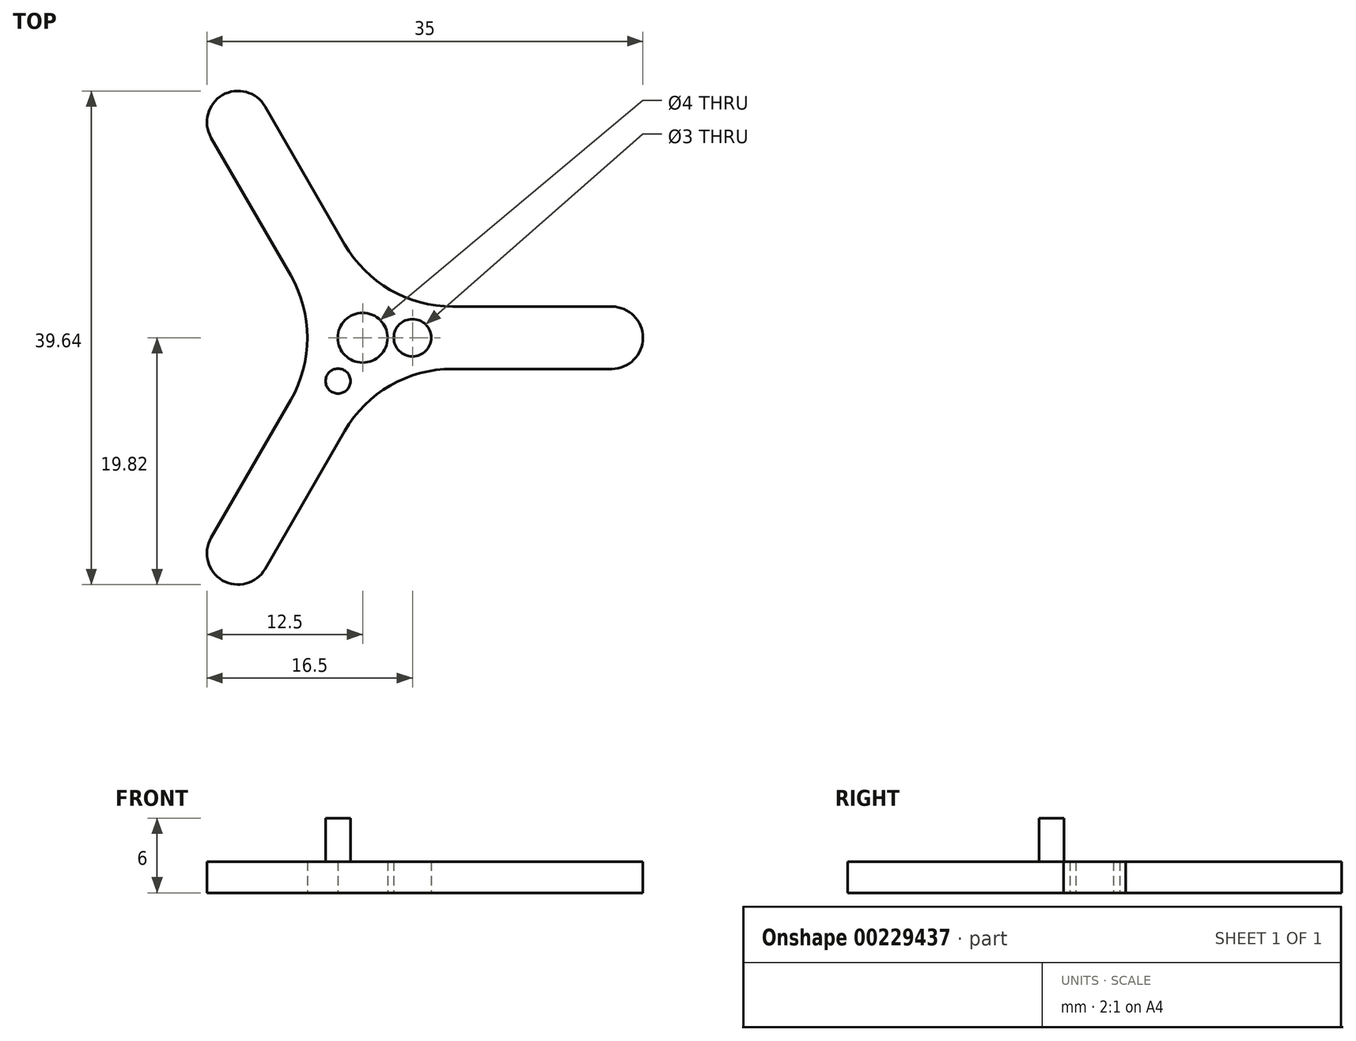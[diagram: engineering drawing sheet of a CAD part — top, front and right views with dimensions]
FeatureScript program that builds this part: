
annotation { "Feature Type Name" : "Feature", "Feature Type Description" : "" }
export const myFeature = defineFeature(function(context is Context, id is Id, definition is map)
    precondition{}
    {
        {
            var Q0;
            Q0=qCreatedBy(makeId("Top.planeOp"),FACE);
            var sketch = newSketch(context, id + "F0", { "sketchPlane" : qUnion([Q0])});
            skCircle(sketch, "E0", {"center": v(20, 0) * mm, "radius": 2.5 * mm});
            skCircle(sketch, "E1", {"center": v(0, 0) * mm, "radius": 2.5 * mm});
            skLineSegment(sketch, "E2", {"start": v(20, 0) * mm, "end": v(0, 0) * mm});
            skLineSegment(sketch, "E3", {"start": v(0, -2.5) * mm, "end": v(20, -2.5) * mm});
            skLineSegment(sketch, "E4.MirrorCS", {"start": v(0, 2.5) * mm, "end": v(20, 2.5) * mm});
            skLineSegment(sketch, "E5.1.1", {"start": v(2.17, 1.25) * mm, "end": v(-7.83, 18.57) * mm});
            skLineSegment(sketch, "E5.1.2", {"start": v(-2.17, -1.25) * mm, "end": v(-12.17, 16.07) * mm});
            skCircle(sketch, "E5.1.3", {"center": v(-10, 17.32) * mm, "radius": 2.5 * mm});
            skLineSegment(sketch, "E5.1.4", {"start": v(-10, 17.32) * mm, "end": v(0, 0) * mm});
            skLineSegment(sketch, "E5.2.1", {"start": v(-2.17, 1.25) * mm, "end": v(-12.17, -16.07) * mm});
            skLineSegment(sketch, "E5.2.2", {"start": v(2.17, -1.25) * mm, "end": v(-7.83, -18.57) * mm});
            skCircle(sketch, "E5.2.3", {"center": v(-10, -17.32) * mm, "radius": 2.5 * mm});
            skLineSegment(sketch, "E5.2.4", {"start": v(-10, -17.32) * mm, "end": v(0, 0) * mm});
            skPoint(sketch, "E6", {"position": v(5, 0) * mm});
            skPoint(sketch, "E7", {"position": v(-2.5, -4.33) * mm});
            skSolve(sketch);
        }
        {
            var Q0;
            Q0 = qSketchRegion(id + "F0", true);
            var Q1;
            {var subQ0=sQuery(id+"F0.wireOp",EDGE,"E1");var subQ4=makeQuery(id+"F0.imprint","INTERSECT",VERTEX,{"derivedFrom":[subQ0,sQuery(id+"F0.wireOp",EDGE,"E5.2.1")]});Q1=makeQuery(id+"F0.imprint","IMPRINT",FACE,{"disambiguationData":[TD([[makeQuery(id+"F0.imprint","IMPRINT",EDGE,{"disambiguationData":[TD([[subQ4,1.0]])],"derivedFrom":subQ0}),1.0]])]});}
            var Q2;
            {var subQ3=sQuery(id+"F0.wireOp",EDGE,"E1");var subQ6=makeQuery(id+"F0.imprint","INTERSECT",VERTEX,{"derivedFrom":[sQuery(id+"F0.wireOp",EDGE,"E5.1.1"),subQ3]});Q2=makeQuery(id+"F0.imprint","IMPRINT",FACE,{"disambiguationData":[TD([[makeQuery(id+"F0.imprint","IMPRINT",EDGE,{"disambiguationData":[TD([[subQ6,1.0]])],"derivedFrom":subQ3}),1.0]])]});}
            var Q3;
            {var subQ0=sQuery(id+"F0.wireOp",EDGE,"E1");var subQ1=makeQuery(id+"F0.imprint","INTERSECT",VERTEX,{"derivedFrom":[sQuery(id+"F0.wireOp",EDGE,"E3"),subQ0]});Q3=makeQuery(id+"F0.imprint","IMPRINT",FACE,{"disambiguationData":[TD([[makeQuery(id+"F0.imprint","IMPRINT",EDGE,{"disambiguationData":[TD([[subQ1,1.0]])],"derivedFrom":subQ0}),1.0]])]});}
            extrude(context, id + "F1", {"entities" : qUnion([Q0, Q1, Q2, Q3]), "depth" : 2.5 * mm});
        }
        {
            var Q0;
            Q0=qCreatedBy(makeId("Top.planeOp"),FACE);
            var sketch = newSketch(context, id + "F2", { "sketchPlane" : qUnion([Q0])});
            skPoint(sketch, "E8", {"position": v(0, 0) * mm});
            skSolve(sketch);
        }
        {
            var Q0;
            Q0=makeQuery(id+"F1.opExtrude","SWEPT_EDGE",EDGE,{"disambiguationData":[OSD([sQuery(id+"F0.wireOp",EDGE,"E3"),sQuery(id+"F0.wireOp",EDGE,"E5.2.2")])]});
            var Q1;
            Q1=makeQuery(id+"F1.opExtrude","SWEPT_EDGE",EDGE,{"disambiguationData":[OSD([sQuery(id+"F0.wireOp",EDGE,"E5.1.2"),sQuery(id+"F0.wireOp",EDGE,"E5.2.1")])]});
            var Q2;
            Q2=makeQuery(id+"F1.opExtrude","SWEPT_EDGE",EDGE,{"disambiguationData":[OSD([sQuery(id+"F0.wireOp",EDGE,"E4.MirrorCS"),sQuery(id+"F0.wireOp",EDGE,"E5.1.1")])]});
            fillet(context, id + "F3", {"entities" : qUnion([Q0, Q1, Q2]), "radius" : 10 * mm, "tangentPropagation" : true, "allowEdgeOverflow" : false});
        }
        {
            var Q0;
            Q0=sQuery(id+"F2.wireOp",VERTEX,"E8");
            var Q1;
            Q1=makeQuery(id+"F1.opExtrude","SWEPT_BODY",BODY,{"disambiguationData":[OSD([sQuery(id+"F0.wireOp",EDGE,"E0"),sQuery(id+"F0.wireOp",EDGE,"E3"),sQuery(id+"F0.wireOp",EDGE,"E4.MirrorCS"),sQuery(id+"F0.wireOp",EDGE,"E5.1.1"),sQuery(id+"F0.wireOp",EDGE,"E5.1.2"),sQuery(id+"F0.wireOp",EDGE,"E5.1.3"),sQuery(id+"F0.wireOp",EDGE,"E5.2.1"),sQuery(id+"F0.wireOp",EDGE,"E5.2.2"),sQuery(id+"F0.wireOp",EDGE,"E5.2.3")])]});
            hole(context, id + "F4", {"style" : HoleStyle.SIMPLE, "endStyle" : HoleEndStyle.THROUGH, "oppositeDirection" : true, "holeDiameter" : 4 * mm, "locations" : qUnion([Q0]), "scope" : qUnion([Q1]), "isTappedThrough" : true});
        }
        {
            var Q0;
            Q0=qCreatedBy(makeId("Top.planeOp"),FACE);
            var sketch = newSketch(context, id + "F5", { "sketchPlane" : qUnion([Q0])});
            skPoint(sketch, "E9", {"position": v(-1.97, -3.48) * mm});
            skCircle(sketch, "E10", {"center": v(-1.97, -3.48) * mm, "radius": 1 * mm});
            skSolve(sketch);
        }
        {
            var Q0;
            Q0=makeQuery(id+"F5.imprint","IMPRINT",FACE,{"disambiguationData":[TD([[makeQuery(id+"F5.imprint","IMPRINT",EDGE,{"derivedFrom":sQuery(id+"F5.wireOp",EDGE,"E10")}),1.0]])]});
            extrude(context, id + "F6", {"entities" : qUnion([Q0]), "operationType" : NewBodyOperationType.ADD, "depth" : 6 * mm});
        }
        {
            var Q0;
            Q0=qCreatedBy(makeId("Top.planeOp"),FACE);
            var sketch = newSketch(context, id + "F7", { "sketchPlane" : qUnion([Q0])});
            skPoint(sketch, "E11", {"position": v(4, 0) * mm});
            skCircle(sketch, "E12", {"center": v(4, 0) * mm, "radius": 1.5 * mm});
            skSolve(sketch);
        }
        {
            var Q0;
            Q0 = qSketchRegion(id + "F7", true);
            extrude(context, id + "F8", {"entities" : qUnion([Q0]), "operationType" : NewBodyOperationType.REMOVE, "depth" : 7 * mm});
        }
    });
